# Revit family: Urinal-American_Standard-Maybrook-6581.001.020
name_source: partatom
category: Plumbing Fixtures
units: mm (PartAtom-declared; Revit-internal decimal feet)

## family parameters
Cut with Voids When Loaded = No
Host = Face
OmniClass Number = 23.45.05.21.11.21
OmniClass Title = Urinals
Part Type = Normal
Room Calculation Point = No
Round Connector Dimension = Use Diameter
Shared = Yes

## types (1)
- 6581.001.020
    Assembly Code = D2010210
    CW Connection = Yes
    CWFU = 5
    Cold Water Connection Diameter = 3/4"
    Cold Water Connection Height = 11 1/2"
    Cold Water Connection Radius = 3/8"
    Cold Water Connection Width = 4 3/4"
    Default Elevation = 24"
    Description = Maybrook 0.125-1.0 gpf Universal Washout Top Spud Urinal
    Finish = Vitreous China-American Standard-020-White
    Flush Rate = 0.125 gpf to 1.0 gpf (0.5 Lpf to 3.8 Lpf)
    HW Connection = No
    HWFU = 0
    Height = 18"
    Installation Type = Wallmount
    Length = 12 3/4"
    Manufacturer = American Standard
    Material = Vitreous China-American Standard-020-White
    Model = 6581.001.020
    Product Documentation Link = https://lixil.cdn.celum.cloud
    Product Page URL = https://www.americanstandard-us.com
    Revised Date = 11/03/2023
    URL = http://www.americanstandard-us.com
    Vent Connection = No
    WFU = 5
    Waste Connection = Yes
    Waste Connection Diameter = 1 1/2"
    Waste Connection Height = 11 1/2"
    Waste Connection Radius = 3/4"
    Width = 12 3/4"

## geometry (parser evidence)
native form markers: Sweep x2
no freeform markers — native parametric forms only
